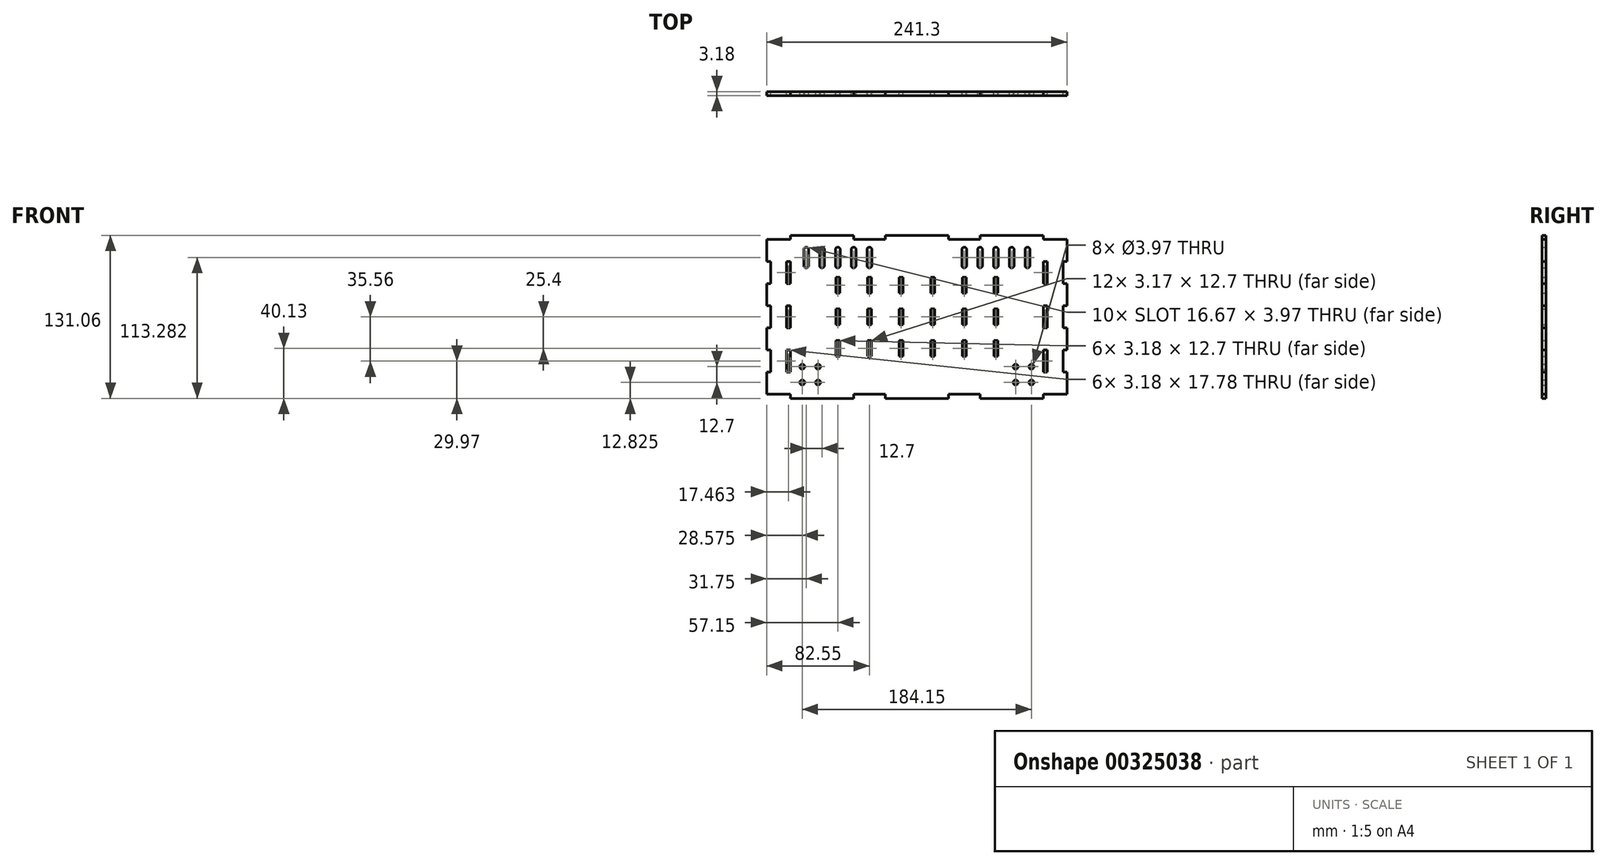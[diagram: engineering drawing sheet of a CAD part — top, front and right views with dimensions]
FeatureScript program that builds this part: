
annotation { "Feature Type Name" : "Feature", "Feature Type Description" : "" }
export const myFeature = defineFeature(function(context is Context, id is Id, definition is map)
    precondition{}
    {
        {
            var Q0;
            Q0=qCreatedBy(makeId("Front.planeOp"),FACE);
            var sketch = newSketch(context, id + "F0", { "sketchPlane" : qUnion([Q0])});
            skLineSegment(sketch, "E0.MirrorCS", {"start": v(-50.8, -65.53) * mm, "end": v(-50.8, -62.23) * mm});
            skLineSegment(sketch, "E1.MirrorCS", {"start": v(25.4, -65.53) * mm, "end": v(25.4, -62.23) * mm});
            skLineSegment(sketch, "E2.MirrorCS", {"start": v(50.8, -65.53) * mm, "end": v(50.8, -62.23) * mm});
            skLineSegment(sketch, "E3.MirrorCS", {"start": v(101.6, -65.53) * mm, "end": v(101.6, -62.23) * mm});
            skLineSegment(sketch, "E4.MirrorCS", {"start": v(-25.4, -65.53) * mm, "end": v(-25.4, -62.23) * mm});
            skLineSegment(sketch, "E5.MirrorCS", {"start": v(101.6, -65.53) * mm, "end": v(50.8, -65.53) * mm});
            skLineSegment(sketch, "E6.MirrorCS", {"start": v(-25.4, -65.53) * mm, "end": v(25.4, -65.53) * mm});
            skLineSegment(sketch, "E7.MirrorCS", {"start": v(-50.8, -65.53) * mm, "end": v(-25.4, -65.53) * mm, "construction": true});
            skLineSegment(sketch, "E8.MirrorCS", {"start": v(-101.6, -65.53) * mm, "end": v(-50.8, -65.53) * mm});
            skLineSegment(sketch, "E9.MirrorCS", {"start": v(-101.6, -65.53) * mm, "end": v(-101.6, -62.23) * mm});
            skLineSegment(sketch, "E10", {"start": v(-120.65, -62.23) * mm, "end": v(-101.6, -62.23) * mm});
            skLineSegment(sketch, "E11.trimOffspring", {"start": v(101.6, -62.23) * mm, "end": v(127, -62.23) * mm});
            skLineSegment(sketch, "E12.trimOffspring", {"start": v(25.4, -62.23) * mm, "end": v(50.8, -62.23) * mm});
            skLineSegment(sketch, "E13.trimOffspring", {"start": v(-50.8, -62.23) * mm, "end": v(-25.4, -62.23) * mm});
            skLineSegment(sketch, "E14", {"start": v(-120.65, 62.23) * mm, "end": v(-120.65, 44.45) * mm});
            skLineSegment(sketch, "E15.MirrorCS", {"start": v(-117.48, 26.67) * mm, "end": v(-117.48, 8.89) * mm, "construction": true});
            skLineSegment(sketch, "E16.MirrorCS", {"start": v(-120.65, -26.67) * mm, "end": v(-120.65, -8.89) * mm});
            skLineSegment(sketch, "E17.MirrorCS", {"start": v(-117.48, 44.45) * mm, "end": v(-117.48, 26.67) * mm});
            skLineSegment(sketch, "E18.MirrorCS", {"start": v(-117.48, -8.9) * mm, "end": v(-117.48, -26.67) * mm, "construction": true});
            skLineSegment(sketch, "E19.MirrorCS", {"start": v(-117.48, 26.67) * mm, "end": v(-120.65, 26.67) * mm});
            skLineSegment(sketch, "E20.MirrorCS", {"start": v(-120.65, 8.89) * mm, "end": v(-117.48, 8.89) * mm});
            skLineSegment(sketch, "E21.MirrorCS", {"start": v(-117.48, 8.89) * mm, "end": v(-117.48, -8.9) * mm});
            skLineSegment(sketch, "E22.MirrorCS", {"start": v(-117.48, -8.89) * mm, "end": v(-120.65, -8.89) * mm});
            skLineSegment(sketch, "E23.MirrorCS", {"start": v(-120.65, -26.67) * mm, "end": v(-117.48, -26.67) * mm});
            skLineSegment(sketch, "E24.MirrorCS", {"start": v(-120.65, 8.89) * mm, "end": v(-120.65, 26.67) * mm});
            skLineSegment(sketch, "E25.MirrorCS", {"start": v(-117.48, -26.67) * mm, "end": v(-117.48, -44.45) * mm});
            skLineSegment(sketch, "E26.MirrorCS", {"start": v(-117.48, -44.45) * mm, "end": v(-120.65, -44.45) * mm});
            skLineSegment(sketch, "E27.MirrorCS", {"start": v(-120.65, 44.45) * mm, "end": v(-117.48, 44.45) * mm});
            skLineSegment(sketch, "E28.trimOffspring", {"start": v(-120.65, 26.67) * mm, "end": v(-120.65, 8.89) * mm});
            skPoint(sketch, "E29.orphan", {"position": v(-120.65, 8.96) * mm});
            skLineSegment(sketch, "E30.trimOffspring", {"start": v(-120.65, -8.89) * mm, "end": v(-120.65, -26.67) * mm});
            skLineSegment(sketch, "E31.trimOffspring", {"start": v(-120.65, -44.45) * mm, "end": v(-120.65, -62.23) * mm});
            skPoint(sketch, "E32", {"position": v(-117.48, 0) * mm});
            skLineSegment(sketch, "E33.MirrorCS", {"start": v(-50.8, 65.53) * mm, "end": v(-25.4, 65.53) * mm, "construction": true});
            skLineSegment(sketch, "E34.MirrorCS", {"start": v(-101.6, 65.53) * mm, "end": v(-101.6, 62.23) * mm});
            skLineSegment(sketch, "E35.MirrorCS", {"start": v(101.6, 62.23) * mm, "end": v(127, 62.23) * mm});
            skLineSegment(sketch, "E36.MirrorCS", {"start": v(25.4, 65.53) * mm, "end": v(25.4, 62.23) * mm});
            skLineSegment(sketch, "E37.MirrorCS", {"start": v(101.6, 65.53) * mm, "end": v(101.6, 62.23) * mm});
            skLineSegment(sketch, "E38.MirrorCS", {"start": v(101.6, 65.53) * mm, "end": v(50.8, 65.53) * mm});
            skLineSegment(sketch, "E39.MirrorCS", {"start": v(-101.6, 65.53) * mm, "end": v(-50.8, 65.53) * mm});
            skLineSegment(sketch, "E40.MirrorCS", {"start": v(-120.65, 62.23) * mm, "end": v(-101.6, 62.23) * mm});
            skLineSegment(sketch, "E41.MirrorCS", {"start": v(25.4, 62.23) * mm, "end": v(50.8, 62.23) * mm});
            skLineSegment(sketch, "E42.MirrorCS", {"start": v(-50.8, 62.23) * mm, "end": v(-25.4, 62.23) * mm});
            skLineSegment(sketch, "E43.MirrorCS", {"start": v(-50.8, 65.53) * mm, "end": v(-50.8, 62.23) * mm});
            skLineSegment(sketch, "E44.MirrorCS", {"start": v(50.8, 65.53) * mm, "end": v(50.8, 62.23) * mm});
            skLineSegment(sketch, "E45.MirrorCS", {"start": v(-25.4, 65.53) * mm, "end": v(-25.4, 62.23) * mm});
            skLineSegment(sketch, "E46.MirrorCS", {"start": v(-25.4, 65.53) * mm, "end": v(25.4, 65.53) * mm});
            skPoint(sketch, "E47", {"position": v(0, 65.53) * mm});
            skLineSegment(sketch, "E48.MirrorCS", {"start": v(117.48, -44.45) * mm, "end": v(120.65, -44.45) * mm});
            skPoint(sketch, "E49.MirrorP", {"position": v(120.65, 8.96) * mm});
            skLineSegment(sketch, "E50.MirrorCS", {"start": v(117.48, 44.45) * mm, "end": v(117.48, 26.67) * mm});
            skLineSegment(sketch, "E51.MirrorCS", {"start": v(117.48, -8.89) * mm, "end": v(120.65, -8.89) * mm});
            skLineSegment(sketch, "E52.MirrorCS", {"start": v(120.65, -26.67) * mm, "end": v(117.48, -26.67) * mm});
            skLineSegment(sketch, "E53.MirrorCS", {"start": v(120.65, 26.67) * mm, "end": v(120.65, 8.89) * mm});
            skLineSegment(sketch, "E54.MirrorCS", {"start": v(120.65, -44.45) * mm, "end": v(120.65, -62.23) * mm});
            skLineSegment(sketch, "E55.MirrorCS", {"start": v(117.48, 26.67) * mm, "end": v(120.65, 26.67) * mm});
            skLineSegment(sketch, "E56.MirrorCS", {"start": v(117.48, -26.67) * mm, "end": v(117.48, -44.45) * mm});
            skLineSegment(sketch, "E57.MirrorCS", {"start": v(120.65, -26.67) * mm, "end": v(120.65, -8.89) * mm});
            skLineSegment(sketch, "E58.MirrorCS", {"start": v(117.48, 8.9) * mm, "end": v(117.48, -8.9) * mm});
            skLineSegment(sketch, "E59.MirrorCS", {"start": v(120.65, 62.23) * mm, "end": v(120.65, 44.45) * mm});
            skLineSegment(sketch, "E60.MirrorCS", {"start": v(120.65, 44.45) * mm, "end": v(117.48, 44.45) * mm});
            skLineSegment(sketch, "E61.MirrorCS", {"start": v(120.65, -8.89) * mm, "end": v(120.65, -26.67) * mm});
            skPoint(sketch, "E62.MirrorP", {"position": v(117.48, 0) * mm});
            skLineSegment(sketch, "E63.MirrorCS", {"start": v(117.48, -8.9) * mm, "end": v(117.48, -26.67) * mm, "construction": true});
            skLineSegment(sketch, "E64.MirrorCS", {"start": v(120.65, 8.89) * mm, "end": v(120.65, 26.67) * mm});
            skLineSegment(sketch, "E65.MirrorCS", {"start": v(117.48, 26.67) * mm, "end": v(117.48, 8.9) * mm, "construction": true});
            skLineSegment(sketch, "E66.MirrorCS", {"start": v(120.65, 8.89) * mm, "end": v(117.48, 8.89) * mm});
            skPoint(sketch, "E67.oppositeSnap0", {"position": v(-119.06, 26.67) * mm});
            skLineSegment(sketch, "E67.bottom", {"start": v(-104.78, 44.45) * mm, "end": v(-101.6, 44.45) * mm});
            skLineSegment(sketch, "E67.top", {"start": v(-104.78, 26.67) * mm, "end": v(-101.6, 26.67) * mm});
            skLineSegment(sketch, "E67.left", {"start": v(-104.78, 44.45) * mm, "end": v(-104.78, 26.67) * mm});
            skLineSegment(sketch, "E67.right", {"start": v(-101.6, 44.45) * mm, "end": v(-101.6, 26.67) * mm});
            skLineSegment(sketch, "E68.bottom", {"start": v(-104.78, 8.89) * mm, "end": v(-101.6, 8.89) * mm});
            skLineSegment(sketch, "E68.top", {"start": v(-104.78, -8.89) * mm, "end": v(-101.6, -8.89) * mm});
            skLineSegment(sketch, "E68.left", {"start": v(-104.78, 8.89) * mm, "end": v(-104.78, -8.89) * mm});
            skLineSegment(sketch, "E68.right", {"start": v(-101.6, 8.89) * mm, "end": v(-101.6, -8.89) * mm});
            skLineSegment(sketch, "E69.bottom", {"start": v(-101.6, -44.45) * mm, "end": v(-104.78, -44.45) * mm});
            skLineSegment(sketch, "E69.top", {"start": v(-101.6, -26.67) * mm, "end": v(-104.78, -26.67) * mm});
            skLineSegment(sketch, "E69.left", {"start": v(-101.6, -44.45) * mm, "end": v(-101.6, -26.67) * mm});
            skLineSegment(sketch, "E69.right", {"start": v(-104.78, -44.45) * mm, "end": v(-104.78, -26.67) * mm});
            skLineSegment(sketch, "E70.MirrorCS", {"start": v(104.78, 8.89) * mm, "end": v(101.6, 8.89) * mm});
            skLineSegment(sketch, "E71.MirrorCS", {"start": v(101.6, -26.67) * mm, "end": v(104.78, -26.67) * mm});
            skLineSegment(sketch, "E72.MirrorCS", {"start": v(104.78, 26.67) * mm, "end": v(101.6, 26.67) * mm});
            skLineSegment(sketch, "E73.MirrorCS", {"start": v(101.6, -44.45) * mm, "end": v(104.78, -44.45) * mm});
            skLineSegment(sketch, "E74.MirrorCS", {"start": v(104.78, 44.45) * mm, "end": v(101.6, 44.45) * mm});
            skLineSegment(sketch, "E75.MirrorCS", {"start": v(104.78, -8.89) * mm, "end": v(101.6, -8.89) * mm});
            skLineSegment(sketch, "E76.MirrorCS", {"start": v(104.78, -44.45) * mm, "end": v(104.78, -26.67) * mm});
            skLineSegment(sketch, "E77.MirrorCS", {"start": v(101.6, 44.45) * mm, "end": v(101.6, 26.67) * mm});
            skLineSegment(sketch, "E78.MirrorCS", {"start": v(101.6, -44.45) * mm, "end": v(101.6, -26.67) * mm});
            skLineSegment(sketch, "E79.MirrorCS", {"start": v(104.78, 44.45) * mm, "end": v(104.78, 26.67) * mm});
            skLineSegment(sketch, "E80.MirrorCS", {"start": v(101.6, 8.89) * mm, "end": v(101.6, -8.89) * mm});
            skLineSegment(sketch, "E81.MirrorCS", {"start": v(104.78, 8.89) * mm, "end": v(104.78, -8.89) * mm});
            skLineSegment(sketch, "E82.bottom", {"start": v(-65.09, -19.05) * mm, "end": v(-61.91, -19.05) * mm});
            skLineSegment(sketch, "E82.top", {"start": v(-65.09, -31.75) * mm, "end": v(-61.91, -31.75) * mm});
            skLineSegment(sketch, "E82.left", {"start": v(-65.09, -19.05) * mm, "end": v(-65.09, -31.75) * mm});
            skLineSegment(sketch, "E82.right", {"start": v(-61.91, -19.05) * mm, "end": v(-61.91, -31.75) * mm});
            skLineSegment(sketch, "E83.0.1.0", {"start": v(-65.09, 6.35) * mm, "end": v(-61.91, 6.35) * mm});
            skLineSegment(sketch, "E83.0.1.1", {"start": v(-65.09, -6.35) * mm, "end": v(-61.91, -6.35) * mm});
            skLineSegment(sketch, "E83.0.1.2", {"start": v(-65.09, 6.35) * mm, "end": v(-65.09, -6.35) * mm});
            skLineSegment(sketch, "E83.0.1.3", {"start": v(-61.91, 6.35) * mm, "end": v(-61.91, -6.35) * mm});
            skLineSegment(sketch, "E83.0.2.0", {"start": v(-65.09, 31.75) * mm, "end": v(-61.91, 31.75) * mm});
            skLineSegment(sketch, "E83.0.2.1", {"start": v(-65.09, 19.05) * mm, "end": v(-61.91, 19.05) * mm});
            skLineSegment(sketch, "E83.0.2.2", {"start": v(-65.09, 31.75) * mm, "end": v(-65.09, 19.05) * mm});
            skLineSegment(sketch, "E83.0.2.3", {"start": v(-61.91, 31.75) * mm, "end": v(-61.91, 19.05) * mm});
            skLineSegment(sketch, "E83.1.0.0", {"start": v(-39.69, -19.05) * mm, "end": v(-36.51, -19.05) * mm});
            skLineSegment(sketch, "E83.1.0.1", {"start": v(-39.69, -31.75) * mm, "end": v(-36.51, -31.75) * mm});
            skLineSegment(sketch, "E83.1.0.2", {"start": v(-39.69, -19.05) * mm, "end": v(-39.69, -31.75) * mm});
            skLineSegment(sketch, "E83.1.0.3", {"start": v(-36.51, -19.05) * mm, "end": v(-36.51, -31.75) * mm});
            skLineSegment(sketch, "E83.1.1.0", {"start": v(-39.69, 6.35) * mm, "end": v(-36.51, 6.35) * mm});
            skLineSegment(sketch, "E83.1.1.1", {"start": v(-39.69, -6.35) * mm, "end": v(-36.51, -6.35) * mm});
            skLineSegment(sketch, "E83.1.1.2", {"start": v(-39.69, 6.35) * mm, "end": v(-39.69, -6.35) * mm});
            skLineSegment(sketch, "E83.1.1.3", {"start": v(-36.51, 6.35) * mm, "end": v(-36.51, -6.35) * mm});
            skLineSegment(sketch, "E83.1.2.0", {"start": v(-39.69, 31.75) * mm, "end": v(-36.51, 31.75) * mm});
            skLineSegment(sketch, "E83.1.2.1", {"start": v(-39.69, 19.05) * mm, "end": v(-36.51, 19.05) * mm});
            skLineSegment(sketch, "E83.1.2.2", {"start": v(-39.69, 31.75) * mm, "end": v(-39.69, 19.05) * mm});
            skLineSegment(sketch, "E83.1.2.3", {"start": v(-36.51, 31.75) * mm, "end": v(-36.51, 19.05) * mm});
            skLineSegment(sketch, "E83.2.0.0", {"start": v(-14.29, -19.05) * mm, "end": v(-11.11, -19.05) * mm});
            skLineSegment(sketch, "E83.2.0.1", {"start": v(-14.29, -31.75) * mm, "end": v(-11.11, -31.75) * mm});
            skLineSegment(sketch, "E83.2.0.2", {"start": v(-14.29, -19.05) * mm, "end": v(-14.29, -31.75) * mm});
            skLineSegment(sketch, "E83.2.0.3", {"start": v(-11.11, -19.05) * mm, "end": v(-11.11, -31.75) * mm});
            skLineSegment(sketch, "E83.2.1.0", {"start": v(-14.29, 6.35) * mm, "end": v(-11.11, 6.35) * mm});
            skLineSegment(sketch, "E83.2.1.1", {"start": v(-14.29, -6.35) * mm, "end": v(-11.11, -6.35) * mm});
            skLineSegment(sketch, "E83.2.1.2", {"start": v(-14.29, 6.35) * mm, "end": v(-14.29, -6.35) * mm});
            skLineSegment(sketch, "E83.2.1.3", {"start": v(-11.11, 6.35) * mm, "end": v(-11.11, -6.35) * mm});
            skLineSegment(sketch, "E83.2.2.0", {"start": v(-14.29, 31.75) * mm, "end": v(-11.11, 31.75) * mm});
            skLineSegment(sketch, "E83.2.2.1", {"start": v(-14.29, 19.05) * mm, "end": v(-11.11, 19.05) * mm});
            skLineSegment(sketch, "E83.2.2.2", {"start": v(-14.29, 31.75) * mm, "end": v(-14.29, 19.05) * mm});
            skLineSegment(sketch, "E83.2.2.3", {"start": v(-11.11, 31.75) * mm, "end": v(-11.11, 19.05) * mm});
            skLineSegment(sketch, "E83.3.0.0", {"start": v(11.11, -19.05) * mm, "end": v(14.29, -19.05) * mm});
            skLineSegment(sketch, "E83.3.0.1", {"start": v(11.11, -31.75) * mm, "end": v(14.29, -31.75) * mm});
            skLineSegment(sketch, "E83.3.0.2", {"start": v(11.11, -19.05) * mm, "end": v(11.11, -31.75) * mm});
            skLineSegment(sketch, "E83.3.0.3", {"start": v(14.29, -19.05) * mm, "end": v(14.29, -31.75) * mm});
            skLineSegment(sketch, "E83.3.1.0", {"start": v(11.11, 6.35) * mm, "end": v(14.29, 6.35) * mm});
            skLineSegment(sketch, "E83.3.1.1", {"start": v(11.11, -6.35) * mm, "end": v(14.29, -6.35) * mm});
            skLineSegment(sketch, "E83.3.1.2", {"start": v(11.11, 6.35) * mm, "end": v(11.11, -6.35) * mm});
            skLineSegment(sketch, "E83.3.1.3", {"start": v(14.29, 6.35) * mm, "end": v(14.29, -6.35) * mm});
            skLineSegment(sketch, "E83.3.2.0", {"start": v(11.11, 31.75) * mm, "end": v(14.29, 31.75) * mm});
            skLineSegment(sketch, "E83.3.2.1", {"start": v(11.11, 19.05) * mm, "end": v(14.29, 19.05) * mm});
            skLineSegment(sketch, "E83.3.2.2", {"start": v(11.11, 31.75) * mm, "end": v(11.11, 19.05) * mm});
            skLineSegment(sketch, "E83.3.2.3", {"start": v(14.29, 31.75) * mm, "end": v(14.29, 19.05) * mm});
            skLineSegment(sketch, "E83.4.0.0", {"start": v(36.51, -19.05) * mm, "end": v(39.69, -19.05) * mm});
            skLineSegment(sketch, "E83.4.0.1", {"start": v(36.51, -31.75) * mm, "end": v(39.69, -31.75) * mm});
            skLineSegment(sketch, "E83.4.0.2", {"start": v(36.51, -19.05) * mm, "end": v(36.51, -31.75) * mm});
            skLineSegment(sketch, "E83.4.0.3", {"start": v(39.69, -19.05) * mm, "end": v(39.69, -31.75) * mm});
            skLineSegment(sketch, "E83.4.1.0", {"start": v(36.51, 6.35) * mm, "end": v(39.69, 6.35) * mm});
            skLineSegment(sketch, "E83.4.1.1", {"start": v(36.51, -6.35) * mm, "end": v(39.69, -6.35) * mm});
            skLineSegment(sketch, "E83.4.1.2", {"start": v(36.51, 6.35) * mm, "end": v(36.51, -6.35) * mm});
            skLineSegment(sketch, "E83.4.1.3", {"start": v(39.69, 6.35) * mm, "end": v(39.69, -6.35) * mm});
            skLineSegment(sketch, "E83.4.2.0", {"start": v(36.51, 31.75) * mm, "end": v(39.69, 31.75) * mm});
            skLineSegment(sketch, "E83.4.2.1", {"start": v(36.51, 19.05) * mm, "end": v(39.69, 19.05) * mm});
            skLineSegment(sketch, "E83.4.2.2", {"start": v(36.51, 31.75) * mm, "end": v(36.51, 19.05) * mm});
            skLineSegment(sketch, "E83.4.2.3", {"start": v(39.69, 31.75) * mm, "end": v(39.69, 19.05) * mm});
            skLineSegment(sketch, "E83.5.0.0", {"start": v(61.91, -19.05) * mm, "end": v(65.09, -19.05) * mm});
            skLineSegment(sketch, "E83.5.0.1", {"start": v(61.91, -31.75) * mm, "end": v(65.09, -31.75) * mm});
            skLineSegment(sketch, "E83.5.0.2", {"start": v(61.91, -19.05) * mm, "end": v(61.91, -31.75) * mm});
            skLineSegment(sketch, "E83.5.0.3", {"start": v(65.09, -19.05) * mm, "end": v(65.09, -31.75) * mm});
            skLineSegment(sketch, "E83.5.1.0", {"start": v(61.91, 6.35) * mm, "end": v(65.09, 6.35) * mm});
            skLineSegment(sketch, "E83.5.1.1", {"start": v(61.91, -6.35) * mm, "end": v(65.09, -6.35) * mm});
            skLineSegment(sketch, "E83.5.1.2", {"start": v(61.91, 6.35) * mm, "end": v(61.91, -6.35) * mm});
            skLineSegment(sketch, "E83.5.1.3", {"start": v(65.09, 6.35) * mm, "end": v(65.09, -6.35) * mm});
            skLineSegment(sketch, "E83.5.2.0", {"start": v(61.91, 31.75) * mm, "end": v(65.09, 31.75) * mm});
            skLineSegment(sketch, "E83.5.2.1", {"start": v(61.91, 19.05) * mm, "end": v(65.09, 19.05) * mm});
            skLineSegment(sketch, "E83.5.2.2", {"start": v(61.91, 31.75) * mm, "end": v(61.91, 19.05) * mm});
            skLineSegment(sketch, "E83.5.2.3", {"start": v(65.09, 31.75) * mm, "end": v(65.09, 19.05) * mm});
            skLineSegment(sketch, "E83.direction1", {"start": v(-65.09, -31.75) * mm, "end": v(-39.69, -31.75) * mm, "construction": true});
            skLineSegment(sketch, "E83.direction2", {"start": v(-65.09, -31.75) * mm, "end": v(-65.09, -6.35) * mm, "construction": true});
            skLineSegment(sketch, "E84", {"start": v(11.11, -25.4) * mm, "end": v(-11.11, -25.4) * mm, "construction": true});
            skPoint(sketch, "E85", {"position": v(0, -25.4) * mm});
            skLineSegment(sketch, "E86", {"start": v(-88.9, 54.1) * mm, "end": v(-38.1, 54.1) * mm, "construction": true});
            skArc(sketch, "E87", {"start": v(-36.12, 54.1) * mm, "mid": v(-38.1, 56.09) * mm, "end": v(-40.08, 54.1) * mm});
            skArc(sketch, "E88", {"start": v(-40.08, 41.4) * mm, "mid": v(-38.1, 39.42) * mm, "end": v(-36.12, 41.4) * mm});
            skLineSegment(sketch, "E89", {"start": v(-36.12, 54.1) * mm, "end": v(-36.12, 41.4) * mm});
            skLineSegment(sketch, "E90", {"start": v(-40.08, 54.1) * mm, "end": v(-40.08, 41.4) * mm});
            skArc(sketch, "E91.1.0.0", {"start": v(-48.82, 54.1) * mm, "mid": v(-50.8, 56.09) * mm, "end": v(-52.78, 54.1) * mm});
            skLineSegment(sketch, "E91.1.0.1", {"start": v(-48.82, 54.1) * mm, "end": v(-48.82, 41.4) * mm});
            skArc(sketch, "E91.1.0.2", {"start": v(-52.78, 41.4) * mm, "mid": v(-50.8, 39.42) * mm, "end": v(-48.82, 41.4) * mm});
            skLineSegment(sketch, "E91.1.0.3", {"start": v(-52.78, 54.1) * mm, "end": v(-52.78, 41.4) * mm});
            skArc(sketch, "E91.2.0.0", {"start": v(-61.52, 54.1) * mm, "mid": v(-63.5, 56.09) * mm, "end": v(-65.48, 54.1) * mm});
            skLineSegment(sketch, "E91.2.0.1", {"start": v(-61.52, 54.1) * mm, "end": v(-61.52, 41.4) * mm});
            skArc(sketch, "E91.2.0.2", {"start": v(-65.48, 41.4) * mm, "mid": v(-63.5, 39.42) * mm, "end": v(-61.52, 41.4) * mm});
            skLineSegment(sketch, "E91.2.0.3", {"start": v(-65.48, 54.1) * mm, "end": v(-65.48, 41.4) * mm});
            skArc(sketch, "E91.3.0.0", {"start": v(-74.22, 54.1) * mm, "mid": v(-76.2, 56.09) * mm, "end": v(-78.18, 54.1) * mm});
            skLineSegment(sketch, "E91.3.0.1", {"start": v(-74.22, 54.1) * mm, "end": v(-74.22, 41.4) * mm});
            skArc(sketch, "E91.3.0.2", {"start": v(-78.18, 41.4) * mm, "mid": v(-76.2, 39.42) * mm, "end": v(-74.22, 41.4) * mm});
            skLineSegment(sketch, "E91.3.0.3", {"start": v(-78.18, 54.1) * mm, "end": v(-78.18, 41.4) * mm});
            skArc(sketch, "E91.4.0.0", {"start": v(-86.92, 54.1) * mm, "mid": v(-88.9, 56.09) * mm, "end": v(-90.88, 54.1) * mm});
            skLineSegment(sketch, "E91.4.0.1", {"start": v(-86.92, 54.1) * mm, "end": v(-86.92, 41.4) * mm});
            skArc(sketch, "E91.4.0.2", {"start": v(-90.88, 41.4) * mm, "mid": v(-88.9, 39.42) * mm, "end": v(-86.92, 41.4) * mm});
            skLineSegment(sketch, "E91.4.0.3", {"start": v(-90.88, 54.1) * mm, "end": v(-90.88, 41.4) * mm});
            skLineSegment(sketch, "E91.direction1", {"start": v(-40.08, 41.4) * mm, "end": v(-52.78, 41.4) * mm, "construction": true});
            skArc(sketch, "E92.MirrorCS", {"start": v(52.78, 41.4) * mm, "mid": v(50.8, 39.42) * mm, "end": v(48.82, 41.4) * mm});
            skArc(sketch, "E93.MirrorCS", {"start": v(86.92, 54.1) * mm, "mid": v(88.9, 56.09) * mm, "end": v(90.88, 54.1) * mm});
            skLineSegment(sketch, "E94.MirrorCS", {"start": v(74.22, 54.1) * mm, "end": v(74.22, 41.4) * mm});
            skLineSegment(sketch, "E95.MirrorCS", {"start": v(36.12, 54.1) * mm, "end": v(36.12, 41.4) * mm});
            skArc(sketch, "E96.MirrorCS", {"start": v(61.52, 54.1) * mm, "mid": v(63.5, 56.09) * mm, "end": v(65.48, 54.1) * mm});
            skArc(sketch, "E97.MirrorCS", {"start": v(90.88, 41.4) * mm, "mid": v(88.9, 39.42) * mm, "end": v(86.92, 41.4) * mm});
            skLineSegment(sketch, "E98.MirrorCS", {"start": v(88.9, 54.1) * mm, "end": v(38.1, 54.1) * mm, "construction": true});
            skArc(sketch, "E99.MirrorCS", {"start": v(48.82, 54.1) * mm, "mid": v(50.8, 56.09) * mm, "end": v(52.78, 54.1) * mm});
            skLineSegment(sketch, "E100.MirrorCS", {"start": v(48.82, 54.1) * mm, "end": v(48.82, 41.4) * mm});
            skArc(sketch, "E101.MirrorCS", {"start": v(65.48, 41.4) * mm, "mid": v(63.5, 39.42) * mm, "end": v(61.52, 41.4) * mm});
            skLineSegment(sketch, "E102.MirrorCS", {"start": v(78.18, 54.1) * mm, "end": v(78.18, 41.4) * mm});
            skLineSegment(sketch, "E103.MirrorCS", {"start": v(40.08, 41.4) * mm, "end": v(52.78, 41.4) * mm, "construction": true});
            skArc(sketch, "E104.MirrorCS", {"start": v(74.22, 54.1) * mm, "mid": v(76.2, 56.09) * mm, "end": v(78.18, 54.1) * mm});
            skArc(sketch, "E105.MirrorCS", {"start": v(40.08, 41.4) * mm, "mid": v(38.1, 39.42) * mm, "end": v(36.12, 41.4) * mm});
            skLineSegment(sketch, "E106.MirrorCS", {"start": v(52.78, 54.1) * mm, "end": v(52.78, 41.4) * mm});
            skLineSegment(sketch, "E107.MirrorCS", {"start": v(86.92, 54.1) * mm, "end": v(86.92, 41.4) * mm});
            skLineSegment(sketch, "E108.MirrorCS", {"start": v(40.08, 54.1) * mm, "end": v(40.08, 41.4) * mm});
            skLineSegment(sketch, "E109.MirrorCS", {"start": v(61.52, 54.1) * mm, "end": v(61.52, 41.4) * mm});
            skArc(sketch, "E110.MirrorCS", {"start": v(78.18, 41.4) * mm, "mid": v(76.2, 39.42) * mm, "end": v(74.22, 41.4) * mm});
            skLineSegment(sketch, "E111.MirrorCS", {"start": v(90.88, 54.1) * mm, "end": v(90.88, 41.4) * mm});
            skLineSegment(sketch, "E112.MirrorCS", {"start": v(65.48, 54.1) * mm, "end": v(65.48, 41.4) * mm});
            skArc(sketch, "E113.MirrorCS", {"start": v(36.12, 54.1) * mm, "mid": v(38.1, 56.09) * mm, "end": v(40.08, 54.1) * mm});
            skLineSegment(sketch, "E114", {"start": v(-101.6, -44.45) * mm, "end": v(-101.6, -62.23) * mm, "construction": true});
            skCircle(sketch, "E115", {"center": v(-92.08, -52.7) * mm, "radius": 1.98 * mm});
            skCircle(sketch, "E116", {"center": v(-79.38, -52.7) * mm, "radius": 1.98 * mm});
            skCircle(sketch, "E117", {"center": v(-79.38, -40) * mm, "radius": 1.98 * mm});
            skCircle(sketch, "E118", {"center": v(-92.08, -40) * mm, "radius": 1.98 * mm});
            skCircle(sketch, "E119.MirrorC", {"center": v(92.08, -40) * mm, "radius": 1.98 * mm});
            skCircle(sketch, "E120.MirrorC", {"center": v(92.08, -52.7) * mm, "radius": 1.98 * mm});
            skCircle(sketch, "E121.MirrorC", {"center": v(79.38, -40) * mm, "radius": 1.98 * mm});
            skCircle(sketch, "E122.MirrorC", {"center": v(79.38, -52.7) * mm, "radius": 1.98 * mm});
            skSolve(sketch);
        }
        {
            var Q0;
            Q0=makeQuery(id+"F0.imprint","IMPRINT",FACE,{"disambiguationData":[TD([[makeQuery(id+"F0.imprint","IMPRINT",EDGE,{"derivedFrom":sQuery(id+"F0.wireOp",EDGE,"E0.MirrorCS")}),1.0]])]});
            extrude(context, id + "F1", {"entities" : qUnion([Q0]), "depth" : 3.17 * mm});
        }
    });
